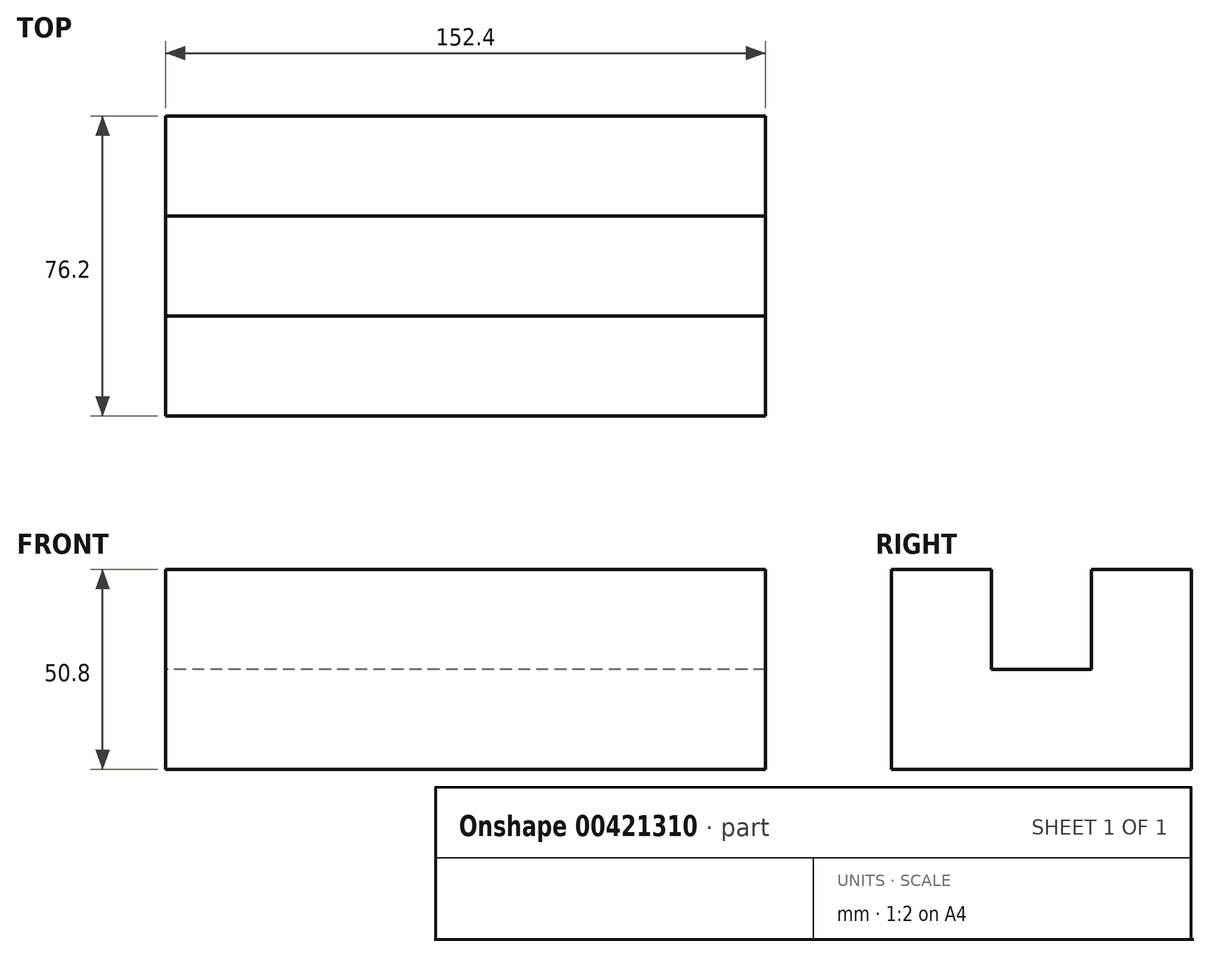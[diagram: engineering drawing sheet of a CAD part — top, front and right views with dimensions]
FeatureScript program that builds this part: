
annotation { "Feature Type Name" : "Feature", "Feature Type Description" : "" }
export const myFeature = defineFeature(function(context is Context, id is Id, definition is map)
    precondition{}
    {
        {
            var Q0;
            Q0=qCreatedBy(makeId("Right.planeOp"),FACE);
            var sketch = newSketch(context, id + "F0", { "sketchPlane" : qUnion([Q0])});
            skLineSegment(sketch, "E0", {"start": v(0, 0) * mm, "end": v(76.2, 0) * mm});
            skLineSegment(sketch, "E1", {"start": v(76.2, 0) * mm, "end": v(76.2, 50.8) * mm});
            skLineSegment(sketch, "E2", {"start": v(0, 0) * mm, "end": v(0, 50.8) * mm});
            skLineSegment(sketch, "E3", {"start": v(0, 50.8) * mm, "end": v(25.4, 50.8) * mm});
            skLineSegment(sketch, "E4", {"start": v(76.2, 50.8) * mm, "end": v(50.8, 50.8) * mm});
            skLineSegment(sketch, "E5", {"start": v(25.4, 50.8) * mm, "end": v(25.4, 25.4) * mm});
            skLineSegment(sketch, "E6", {"start": v(25.4, 25.4) * mm, "end": v(50.8, 25.4) * mm});
            skLineSegment(sketch, "E7", {"start": v(50.8, 50.8) * mm, "end": v(50.8, 25.4) * mm});
            skSolve(sketch);
        }
        {
            var Q0;
            Q0=makeQuery(id+"F0.imprint","IMPRINT",FACE,{"disambiguationData":[TD([[makeQuery(id+"F0.imprint","IMPRINT",EDGE,{"derivedFrom":sQuery(id+"F0.wireOp",EDGE,"E0")}),1.0]])]});
            extrude(context, id + "F1", {"entities" : qUnion([Q0]), "depth" : 152.4 * mm});
        }
    });
